# Revit family: Deca_Caixa acoplada com acionamento Duo_Quadratta_CD.44F
name_source: partatom
category: Plumbing Fixtures
units: mm (PartAtom-declared; Revit-internal decimal feet)

## family parameters
Cut with Voids When Loaded = No
Host = Face
Part Type = Normal
Room Calculation Point = No
Round Connector Dimension = Use Diameter
Shared = No

## types (1)
- CD.44F.17_Branco
    Acompanha o Produto = Caixa Acoplada Interna + Fixação
    Aprovado por = quattroD
    Atendimento ao Cliente = 0800-0117073
    Categoria = BACIAS E BIDES
    Composição Anel Vedação = -
    Composição Assento = -
    Composição Básica = Argila, feldspato, caulim, vidrados e corantes inorgânicos.
    Composição Componente = Liga de cobre (bronze e latão), elastômeros e plásticos de engenharia.
    Consumo = 6 / 3 (lpf) - 1,6 / 0,8 (gpf)
    Cor Interna = -
    Cor Principal = Branco
    Cor Secundária = -
    Cores Componente = Cromado
    Criado por = quattroD
    Código Pai = CD.44F
    Default Elevation = 0 m
    Description = Caixa acoplada com acionamento Duo
    Informações Complementares = -
    Itens de Instalação = -
    Linha = Quadratta
    Manufacturer = Deca
    Material = Deca_Branco
    Model = CD.44F.17
    Norma = NBR15491
    Peso Líquido (Kg) = 15.252
    Pressão máx. funcionamento = 40 MCA
    Pressão mín. Aquec. Acúmulo = -
    Pressão mín. Aquec. Passagem = -
    Pressão mín. funcionamento = 2 MCA
    Saída de Esgoto = -
    Segmento = Banheiro Luxo
    Tipo de dispositivo economizador = -
    Tipo de mecanismo utilizado = -
    Tipo de rosca de entrada = -
    Tipo de rosca de saída = -
    URL = www.deca.com.br
    Vazão na Pressão máx. (L/min) = -
    Vazão na Pressão mín. (L/min) = -

## geometry (parser evidence)
native form markers: Sweep x2
no freeform markers — native parametric forms only
